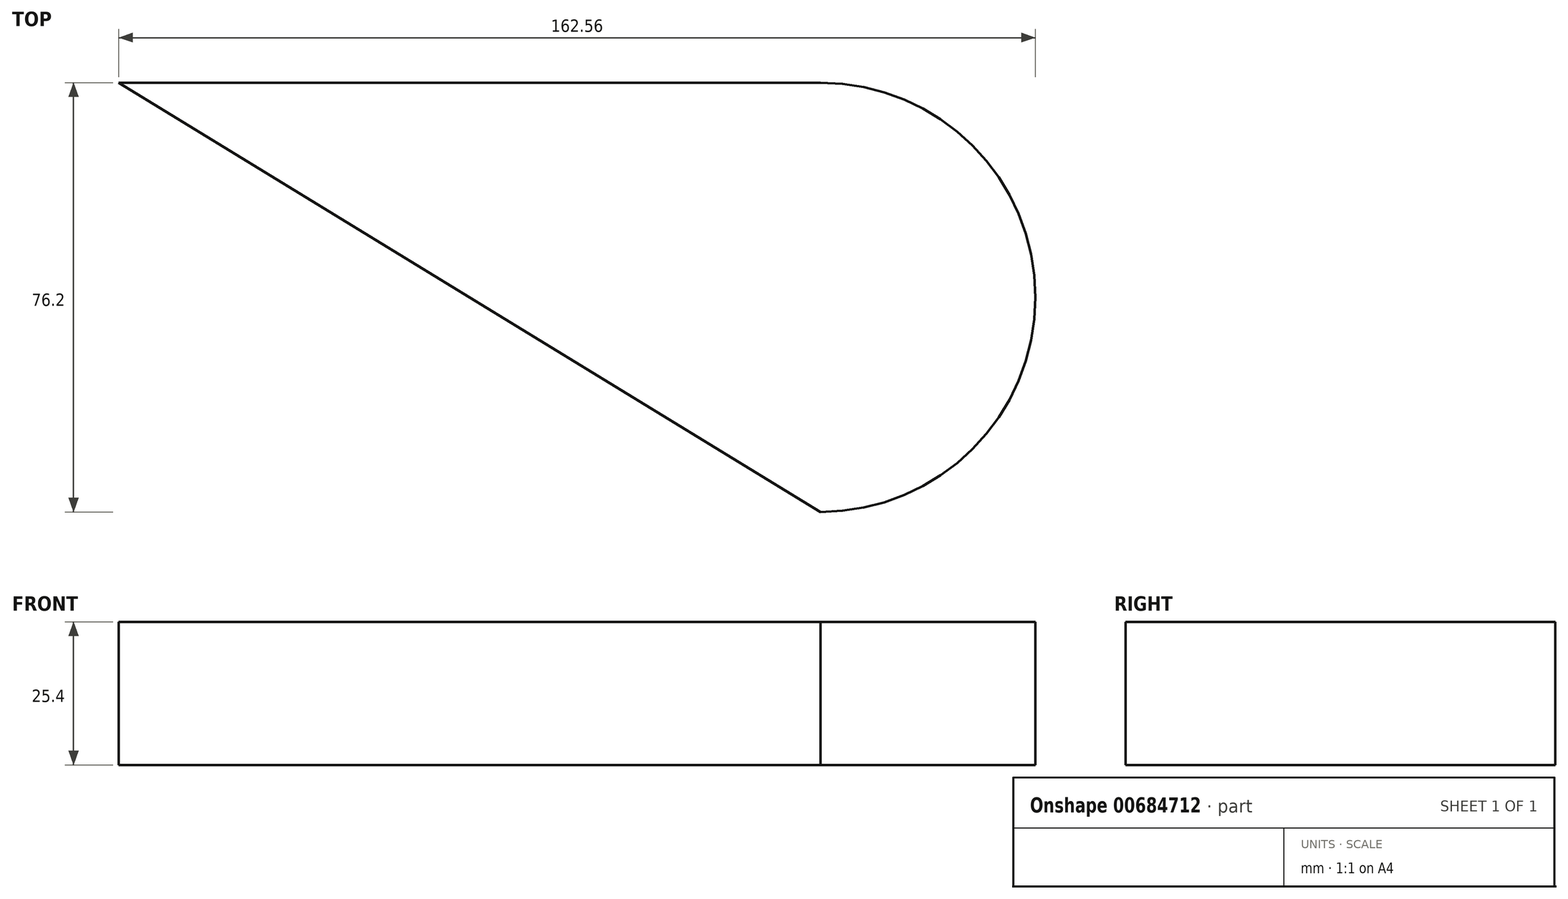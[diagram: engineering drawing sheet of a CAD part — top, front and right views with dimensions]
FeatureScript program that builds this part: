
annotation { "Feature Type Name" : "Feature", "Feature Type Description" : "" }
export const myFeature = defineFeature(function(context is Context, id is Id, definition is map)
    precondition{}
    {
        {
            var Q0;
            Q0=qCreatedBy(makeId("Top.planeOp"),FACE);
            var sketch = newSketch(context, id + "F0", { "sketchPlane" : qUnion([Q0])});
            skLineSegment(sketch, "E0", {"start": v(-67.68, 45.88) * mm, "end": v(56.78, 45.88) * mm});
            skLineSegment(sketch, "E1", {"start": v(56.78, 45.88) * mm, "end": v(56.78, -30.32) * mm});
            skLineSegment(sketch, "E2", {"start": v(-67.68, 45.88) * mm, "end": v(56.78, -30.32) * mm});
            skLineSegment(sketch, "E3", {"start": v(56.78, 45.88) * mm, "end": v(56.78, 7.78) * mm});
            skLineSegment(sketch, "E4", {"start": v(56.78, 7.78) * mm, "end": v(94.88, 7.78) * mm});
            skArc(sketch, "E5", {"start": v(94.88, 7.78) * mm, "mid": v(83.72, 34.72) * mm, "end": v(56.78, 45.88) * mm});
            skArc(sketch, "E6", {"start": v(56.78, -30.32) * mm, "mid": v(83.72, -19.17) * mm, "end": v(94.88, 7.78) * mm});
            skSolve(sketch);
        }
        {
            var Q0;
            Q0 = qSketchRegion(id + "F0", true);
            extrude(context, id + "F1", {"entities" : qUnion([Q0]), "depth" : 25.4 * mm, "offsetDistance" : 25.4 * mm});
        }
    });
